# Revit family: SW2024
name_source: partatom
category: Generic Models
revit_build: Autodesk Revit 2014 (Build: 20130308_1515(x64)
units: mm (PartAtom-declared; Revit-internal decimal feet)

## types (1)
- SW2024
    Codes/Standards = • Meets and exceeds ASME A112.4.2, ASME
A112.18.1/CSA B125.1, UL 1431, CSA C22.2 #68
• Certifications: IAPMO(cUPC), State of
Massachusetts, City of Los Angeles and others
• Code Compliance: UPC, IPC, NSPC, NPC Canada,
and others
    Colors/Finishes = Standard  #01 Cotton
    Manufacturer = TOTO USA
    Model = SW2024 - Elongated front
    Specifications = • Power Rating: AC 120V-60Hz, 292W
• Power Cord: Maximum length:
3.94 ft/120 cm, 3 prong
grounded plug
• Water Feature: Adjustable Water
Flow Rate:
Front washing -
9.8-14.5 oz/min
Rear washing -
9.1 -14.5 oz/min
Soft Rear - from
9.1 -14.5 oz/min
• Washing Spray Temp: Minimum: 86°F/30°C
Maximum: 104˚F/40˚C
• Safety Device: Thermal fuse
• Seat Warming Feature: Surface Temperature:
Minimum: 82˚F/28˚C
Maximum: 97˚F/36˚C
• Safety Device: Thermal fuse
• Water Supply Pressure:Minimum: 7.25 psi
Maximum: 108.75 psi
• Ambient Temperature: Range:
32˚F/0˚C to 104˚F/40˚C
• Warranty: One Year Limited Warranty
• Shipping dimensions: A200 Elongated –
23 ½” x 19” x 9”
• Shipping weight: A200 Elongated – 15lbs
    Unit Material = Finish - TOTO - Cotton 01

## geometry (parser evidence)
native form markers: Sweep x1
no freeform markers — native parametric forms only
